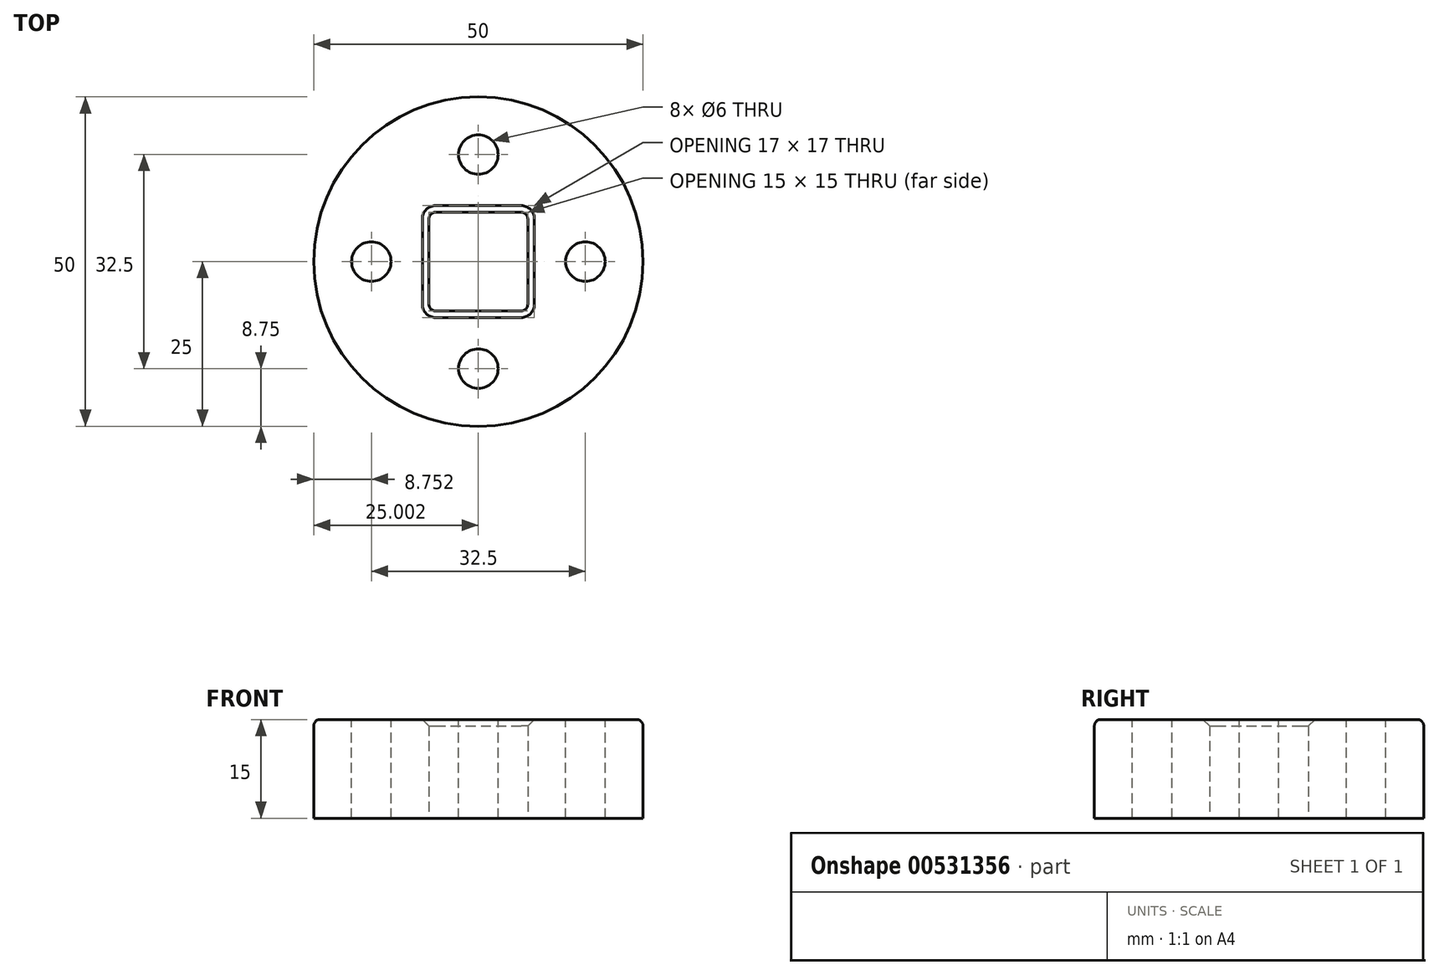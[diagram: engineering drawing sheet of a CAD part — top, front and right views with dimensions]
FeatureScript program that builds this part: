
annotation { "Feature Type Name" : "Feature", "Feature Type Description" : "" }
export const myFeature = defineFeature(function(context is Context, id is Id, definition is map)
    precondition{}
    {
        {
            var Q0;
            Q0=qCreatedBy(makeId("Top.planeOp"),FACE);
            var sketch = newSketch(context, id + "F0", { "sketchPlane" : qUnion([Q0])});
            skCircle(sketch, "E0", {"center": v(-0.02, 0.12) * mm, "radius": 25 * mm});
            skLineSegment(sketch, "E1.bottom", {"start": v(-6.52, -7.38) * mm, "end": v(6.48, -7.38) * mm});
            skLineSegment(sketch, "E1.top", {"start": v(-6.52, 7.62) * mm, "end": v(6.48, 7.62) * mm});
            skLineSegment(sketch, "E1.left", {"start": v(-7.52, -6.38) * mm, "end": v(-7.52, 6.62) * mm});
            skLineSegment(sketch, "E1.right", {"start": v(7.48, -6.38) * mm, "end": v(7.48, 6.62) * mm});
            skPoint(sketch, "E2.visualSharp", {"position": v(-7.52, 7.62) * mm});
            skArc(sketch, "E2.filletArc", {"start": v(-6.52, 7.62) * mm, "mid": v(-7.23, 7.33) * mm, "end": v(-7.52, 6.62) * mm});
            skPoint(sketch, "E3.visualSharp", {"position": v(7.48, 7.62) * mm});
            skArc(sketch, "E3.filletArc", {"start": v(7.48, 6.62) * mm, "mid": v(7.19, 7.33) * mm, "end": v(6.48, 7.62) * mm});
            skPoint(sketch, "E4.visualSharp", {"position": v(7.48, -7.38) * mm});
            skArc(sketch, "E4.filletArc", {"start": v(6.48, -7.38) * mm, "mid": v(7.19, -7.09) * mm, "end": v(7.48, -6.38) * mm});
            skPoint(sketch, "E5.visualSharp", {"position": v(-7.52, -7.38) * mm});
            skArc(sketch, "E5.filletArc", {"start": v(-7.52, -6.38) * mm, "mid": v(-7.23, -7.09) * mm, "end": v(-6.52, -7.38) * mm});
            skSolve(sketch);
        }
        {
            var Q0;
            Q0=makeQuery(id+"F0.imprint","IMPRINT",FACE,{"disambiguationData":[TD([[makeQuery(id+"F0.imprint","IMPRINT",EDGE,{"derivedFrom":sQuery(id+"F0.wireOp",EDGE,"E0")}),1.0]])]});
            extrude(context, id + "F1", {"entities" : qUnion([Q0]), "depth" : 15 * mm, "offsetDistance" : 25 * mm});
        }
        {
            var Q0;
            Q0=makeQuery(id+"F1.opExtrude","CAP_FACE",FACE,{"disambiguationData":[OSD([sQuery(id+"F0.wireOp",EDGE,"E0"),sQuery(id+"F0.wireOp",EDGE,"E1.bottom"),sQuery(id+"F0.wireOp",EDGE,"E1.top"),sQuery(id+"F0.wireOp",EDGE,"E1.left"),sQuery(id+"F0.wireOp",EDGE,"E1.right")])],"isStart":false});
            var sketch = newSketch(context, id + "F2", { "sketchPlane" : qUnion([Q0])});
            skCircle(sketch, "E6", {"center": v(-0.02, 16.37) * mm, "radius": 3 * mm});
            skPoint(sketch, "E6.centerSnap0", {"position": v(-0.02, 7.62) * mm});
            skCircle(sketch, "E7", {"center": v(16.23, 0.12) * mm, "radius": 3 * mm});
            skPoint(sketch, "E7.centerSnap0", {"position": v(7.48, 0.12) * mm});
            skCircle(sketch, "E8", {"center": v(-0.02, -16.13) * mm, "radius": 3 * mm});
            skPoint(sketch, "E8.centerSnap0", {"position": v(-0.02, -7.38) * mm});
            skCircle(sketch, "E9", {"center": v(-16.27, 0.12) * mm, "radius": 3 * mm});
            skPoint(sketch, "E9.centerSnap0", {"position": v(-7.52, 0.12) * mm});
            skSolve(sketch);
        }
        {
            var Q0;
            Q0=makeQuery(id+"F2.imprint","IMPRINT",FACE,{"disambiguationData":[TD([[makeQuery(id+"F2.imprint","IMPRINT",EDGE,{"derivedFrom":sQuery(id+"F2.wireOp",EDGE,"E8")}),1.0]])]});
            var Q1;
            Q1=makeQuery(id+"F2.imprint","IMPRINT",FACE,{"disambiguationData":[TD([[makeQuery(id+"F2.imprint","IMPRINT",EDGE,{"derivedFrom":sQuery(id+"F2.wireOp",EDGE,"E7")}),1.0]])]});
            var Q2;
            Q2=makeQuery(id+"F2.imprint","IMPRINT",FACE,{"disambiguationData":[TD([[makeQuery(id+"F2.imprint","IMPRINT",EDGE,{"derivedFrom":sQuery(id+"F2.wireOp",EDGE,"E6")}),1.0]])]});
            var Q3;
            Q3=makeQuery(id+"F2.imprint","IMPRINT",FACE,{"disambiguationData":[TD([[makeQuery(id+"F2.imprint","IMPRINT",EDGE,{"derivedFrom":sQuery(id+"F2.wireOp",EDGE,"E9")}),1.0]])]});
            var Q4;
            Q4=sQuery(id+"F2.wireOp",EDGE,"E8");
            extrude(context, id + "F3", {"entities" : qUnion([Q0, Q1, Q2, Q3]), "operationType" : NewBodyOperationType.REMOVE, "surfaceEntities" : qUnion([Q4]), "oppositeDirection" : true, "depth" : 15 * mm, "offsetDistance" : 25 * mm});
        }
        {
            var Q0;
            Q0=makeQuery(id+"F1.opExtrude","CAP_EDGE",EDGE,{"disambiguationData":[OSD([sQuery(id+"F0.wireOp",EDGE,"E0")])],"isStart":false});
            var Q1;
            Q1=makeQuery(id+"F3.boolean.opBoolean","COPY",EDGE,{"derivedFrom":makeQuery(id+"F3.opExtrude","CAP_EDGE",EDGE,{"disambiguationData":[OSD([sQuery(id+"F2.wireOp",EDGE,"E9")])],"isStart":true})});
            var Q2;
            Q2=makeQuery(id+"F3.boolean.opBoolean","COPY",EDGE,{"derivedFrom":makeQuery(id+"F3.opExtrude","CAP_EDGE",EDGE,{"disambiguationData":[OSD([sQuery(id+"F2.wireOp",EDGE,"E6")])],"isStart":true})});
            var Q3;
            Q3=makeQuery(id+"F3.boolean.opBoolean","COPY",EDGE,{"derivedFrom":makeQuery(id+"F3.opExtrude","CAP_EDGE",EDGE,{"disambiguationData":[OSD([sQuery(id+"F2.wireOp",EDGE,"E8")])],"isStart":true})});
            var Q4;
            Q4=makeQuery(id+"F3.boolean.opBoolean","COPY",EDGE,{"derivedFrom":makeQuery(id+"F3.opExtrude","CAP_EDGE",EDGE,{"disambiguationData":[OSD([sQuery(id+"F2.wireOp",EDGE,"E7")])],"isStart":true})});
            fillet(context, id + "F4", {"entities" : qUnion([Q0, Q1, Q2, Q3, Q4]), "radius" : 1 * mm, "tangentPropagation" : true, "allowEdgeOverflow" : false});
        }
        {
            var Q0;
            Q0=makeQuery(id+"F1.opExtrude","CAP_EDGE",EDGE,{"disambiguationData":[OSD([sQuery(id+"F0.wireOp",EDGE,"E1.bottom")])],"isStart":false});
            var Q1;
            Q1=makeQuery(id+"F1.opExtrude","CAP_EDGE",EDGE,{"disambiguationData":[OSD([sQuery(id+"F0.wireOp",EDGE,"E1.right")])],"isStart":false});
            var Q2;
            Q2=makeQuery(id+"F1.opExtrude","CAP_EDGE",EDGE,{"disambiguationData":[OSD([sQuery(id+"F0.wireOp",EDGE,"E1.top")])],"isStart":false});
            var Q3;
            Q3=makeQuery(id+"F1.opExtrude","CAP_EDGE",EDGE,{"disambiguationData":[OSD([sQuery(id+"F0.wireOp",EDGE,"E1.left")])],"isStart":false});
            chamfer(context, id + "F5", {"entities" : qUnion([Q0, Q1, Q2, Q3]), "width" : 1 * mm, "tangentPropagation" : true});
        }
    });
